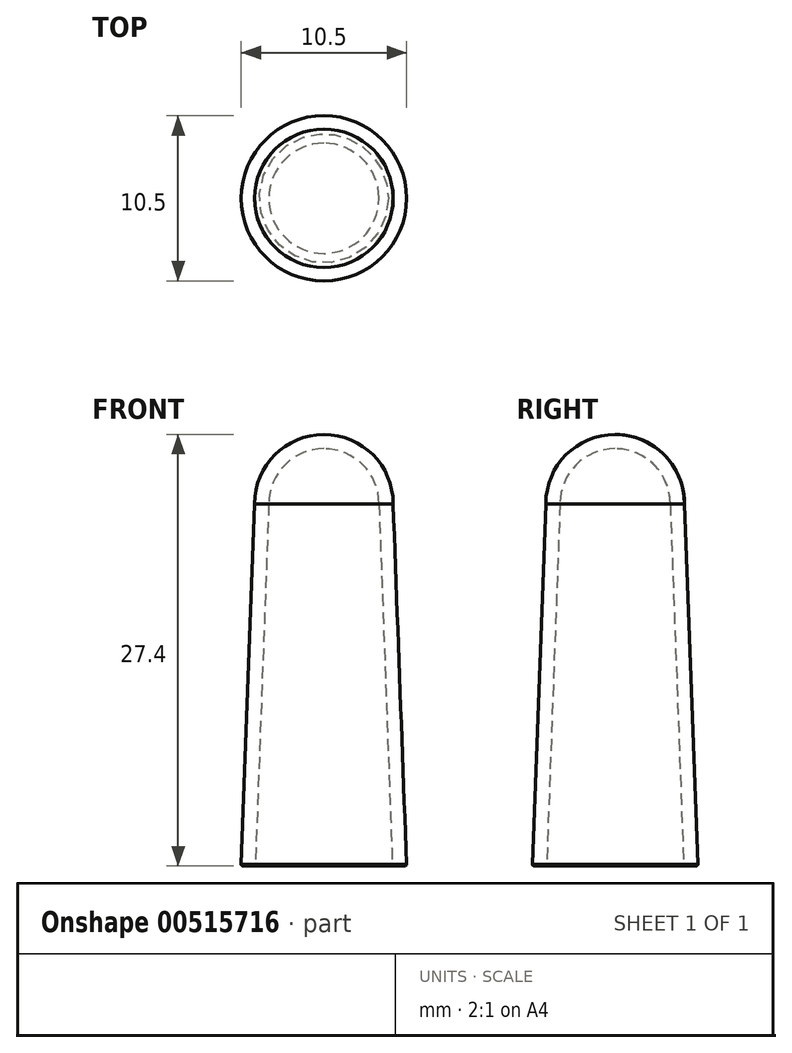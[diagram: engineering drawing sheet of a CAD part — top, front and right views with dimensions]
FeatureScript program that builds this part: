
annotation { "Feature Type Name" : "Feature", "Feature Type Description" : "" }
export const myFeature = defineFeature(function(context is Context, id is Id, definition is map)
    precondition{}
    {
        {
            var Q0;
            Q0=qCreatedBy(makeId("Right.planeOp"),FACE);
            var sketch = newSketch(context, id + "F0", { "sketchPlane" : qUnion([Q0])});
            skLineSegment(sketch, "E0", {"start": v(0, 27.4) * mm, "end": v(0, 26.5) * mm});
            skArc(sketch, "E1", {"start": v(0, 27.4) * mm, "mid": v(-3.11, 26.11) * mm, "end": v(-4.4, 23) * mm});
            skArc(sketch, "E2", {"start": v(0, 26.5) * mm, "mid": v(-2.47, 25.47) * mm, "end": v(-3.5, 23) * mm});
            skArc(sketch, "E3", {"start": v(-4.1, 0.05) * mm, "mid": v(-4.1, 0.09) * mm, "end": v(-4.14, 0.1) * mm});
            skArc(sketch, "E4", {"start": v(-4.1, 0.05) * mm, "mid": v(-4.1, 0.01) * mm, "end": v(-4.14, 0) * mm});
            skLineSegment(sketch, "E5", {"start": v(-4.14, 0.1) * mm, "end": v(-4.35, 0.1) * mm});
            skLineSegment(sketch, "E6", {"start": v(-4.14, 0) * mm, "end": v(-4.35, 0) * mm});
            skLineSegment(sketch, "E7", {"start": v(-4.35, 0.1) * mm, "end": v(-3.5, 23) * mm});
            skLineSegment(sketch, "E8", {"start": v(-4.4, 23) * mm, "end": v(-5.25, 0.1) * mm});
            skArc(sketch, "E9", {"start": v(-5.25, 0.1) * mm, "mid": v(-5.22, 0.03) * mm, "end": v(-5.15, 0) * mm});
            skLineSegment(sketch, "E10", {"start": v(-5.15, 0) * mm, "end": v(-4.35, 0) * mm});
            skLineSegment(sketch, "E11", {"start": v(0, 27.4) * mm, "end": v(0, 0) * mm});
            skSolve(sketch);
        }
        {
            var Q0;
            {var subQ0=sQuery(id+"F0.wireOp",EDGE,"E1");Q0=makeQuery(id+"F0.imprint","IMPRINT",FACE,{"disambiguationData":[TD([[makeQuery(id+"F0.imprint","IMPRINT",EDGE,{"derivedFrom":subQ0}),1.0]])]});}
            var Q1;
            Q1=sQuery(id+"F0.wireOp",EDGE,"E11");
            revolve(context, id + "F1", {"entities" : qUnion([Q0]), "axis" : qUnion([Q1]), "revolveType" : RevolveType.FULL});
        }
    });
